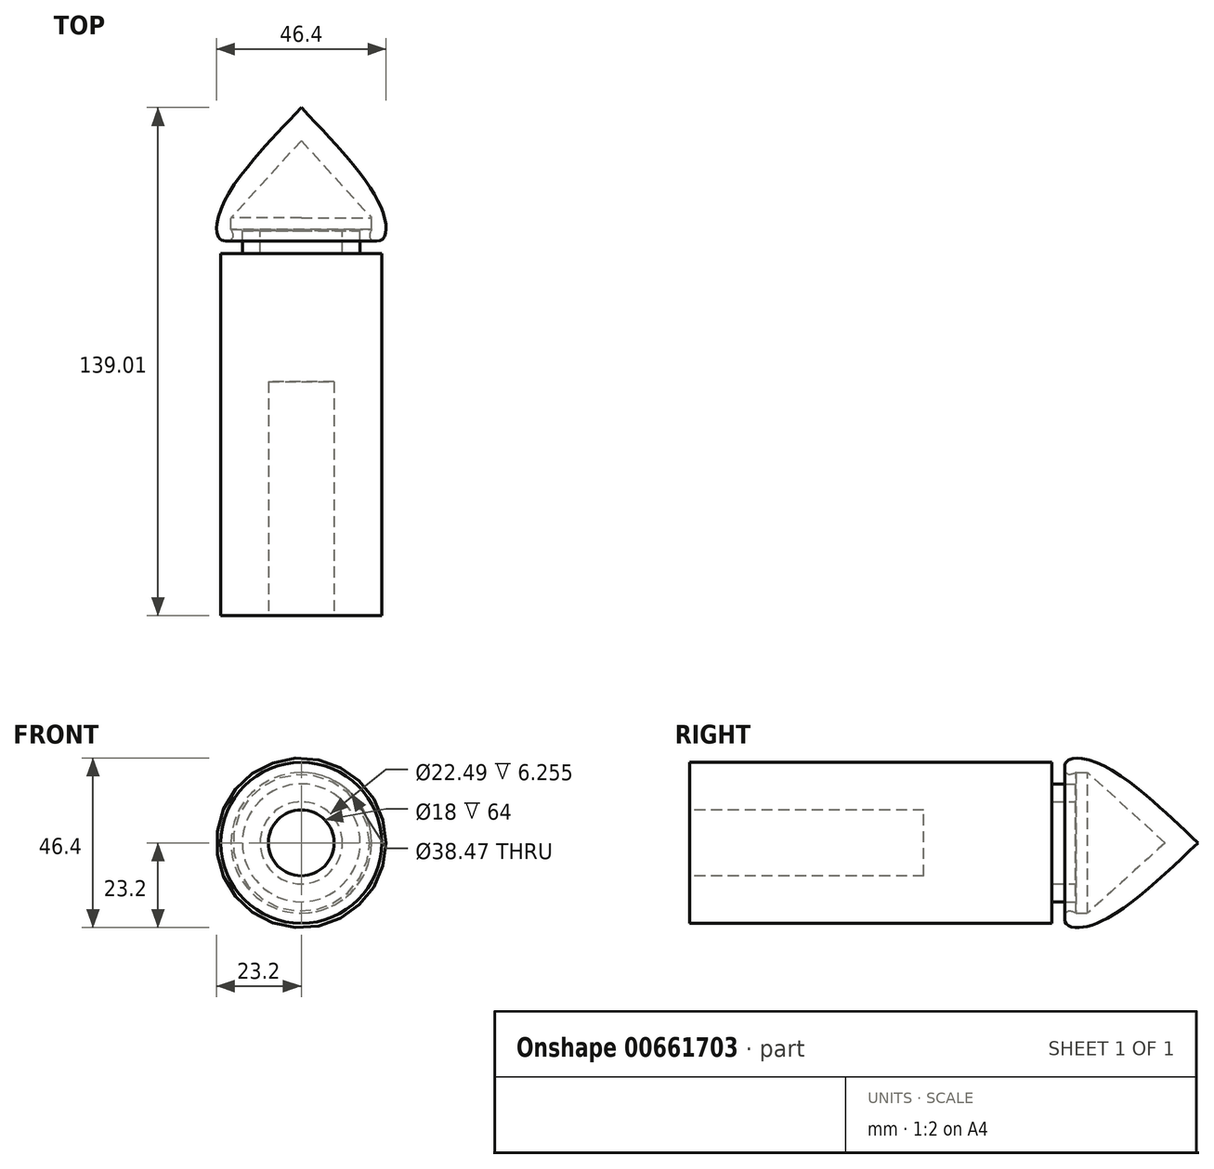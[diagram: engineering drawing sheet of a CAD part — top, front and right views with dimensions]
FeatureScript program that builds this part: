
annotation { "Feature Type Name" : "Feature", "Feature Type Description" : "" }
export const myFeature = defineFeature(function(context is Context, id is Id, definition is map)
    precondition{}
    {
        {
            var Q0;
            Q0=qCreatedBy(makeId("Top.planeOp"),FACE);
            var sketch = newSketch(context, id + "F0", { "sketchPlane" : qUnion([Q0])});
            skLineSegment(sketch, "E0", {"start": v(0, 74.84) * mm, "end": v(0, -76.52) * mm});
            skLineSegment(sketch, "E1", {"start": v(22.02, -68.88) * mm, "end": v(22.02, 30.17) * mm});
            skLineSegment(sketch, "E2", {"start": v(22.02, 30.17) * mm, "end": v(16.1, 30.17) * mm});
            skLineSegment(sketch, "E3", {"start": v(16.1, 30.17) * mm, "end": v(16.1, 36.42) * mm});
            skLineSegment(sketch, "E4", {"start": v(16.1, 36.42) * mm, "end": v(11.24, 36.42) * mm});
            skLineSegment(sketch, "E5", {"start": v(11.24, 36.42) * mm, "end": v(11.24, 30.17) * mm});
            skLineSegment(sketch, "E6", {"start": v(11.24, 30.17) * mm, "end": v(0, 30.17) * mm});
            skFitSpline(sketch, "E7", {"points": [v(19.24, 36.77) * mm, v(18.89, 34.34) * mm, v(22.02, 33.99) * mm, v(22.02, 42.33) * mm, v(0, 70.13) * mm], "startDerivative": vector(-9.4, -21.31) * mm, "endDerivative": vector(-57.83, 60.75) * mm});
            skLineSegment(sketch, "E8", {"start": v(19.24, 36.77) * mm, "end": v(19.24, 39.9) * mm});
            skLineSegment(sketch, "E9", {"start": v(19.24, 39.9) * mm, "end": v(0, 61.1) * mm});
            skLineSegment(sketch, "E10", {"start": v(22.02, -68.88) * mm, "end": v(0, -68.88) * mm});
            skSolve(sketch);
        }
        {
            var Q0;
            Q0 = qSketchRegion(id + "F0", true);
            var Q1;
            Q1=sQuery(id+"F0.wireOp",EDGE,"E0");
            revolve(context, id + "F1", {"entities" : qUnion([Q0]), "axis" : qUnion([Q1]), "revolveType" : RevolveType.FULL});
        }
        {
            var Q0;
            Q0=makeQuery(id+"F1.opRevolve","SWEPT_FACE",FACE,{"disambiguationData":[OSD([sQuery(id+"F0.wireOp",EDGE,"E10")])]});
            var sketch = newSketch(context, id + "F2", { "sketchPlane" : qUnion([Q0])});
            skCircle(sketch, "E11", {"center": v(0, 0) * mm, "radius": 9 * mm});
            skSolve(sketch);
        }
        {
            var Q0;
            Q0=makeQuery(id+"F2.imprint","IMPRINT",FACE,{"disambiguationData":[TD([[makeQuery(id+"F2.imprint","IMPRINT",EDGE,{"derivedFrom":sQuery(id+"F2.wireOp",EDGE,"E11")}),1.0]])]});
            extrude(context, id + "F3", {"entities" : qUnion([Q0]), "operationType" : NewBodyOperationType.REMOVE, "oppositeDirection" : true, "depth" : 64 * mm, "offsetDistance" : 25 * mm});
        }
    });
